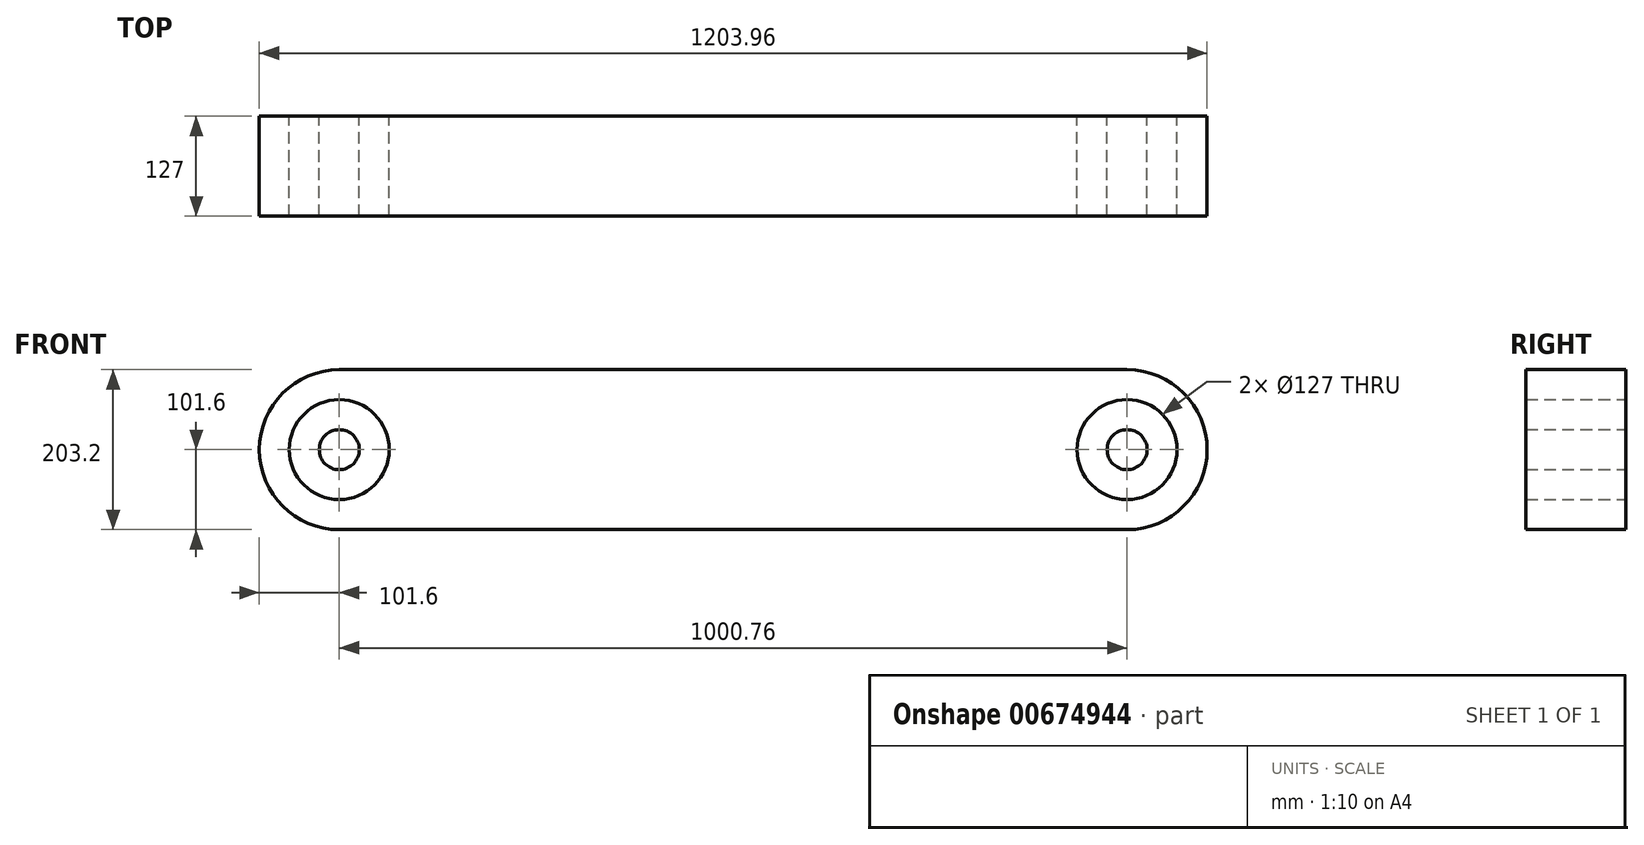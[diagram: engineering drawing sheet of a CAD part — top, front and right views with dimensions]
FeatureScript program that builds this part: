
annotation { "Feature Type Name" : "Feature", "Feature Type Description" : "" }
export const myFeature = defineFeature(function(context is Context, id is Id, definition is map)
    precondition{}
    {
        {
            var Q0;
            Q0=qCreatedBy(makeId("Front.planeOp"),FACE);
            var sketch = newSketch(context, id + "F0", { "sketchPlane" : qUnion([Q0])});
            skLineSegment(sketch, "E0.bottom", {"start": v(0, 0) * mm, "end": v(1000.76, 0) * mm});
            skLineSegment(sketch, "E0.top", {"start": v(0, 203.2) * mm, "end": v(1000.76, 203.2) * mm});
            skArc(sketch, "E1", {"start": v(0, 203.2) * mm, "mid": v(-101.6, 101.6) * mm, "end": v(0, 0) * mm});
            skArc(sketch, "E2", {"start": v(1000.76, 0) * mm, "mid": v(1102.36, 101.6) * mm, "end": v(1000.76, 203.2) * mm});
            skCircle(sketch, "E3", {"center": v(0, 101.6) * mm, "radius": 63.5 * mm});
            skCircle(sketch, "E4", {"center": v(1000.76, 101.6) * mm, "radius": 63.5 * mm});
            skCircle(sketch, "E5", {"center": v(1000.76, 101.6) * mm, "radius": 25.4 * mm});
            skCircle(sketch, "E6", {"center": v(0, 101.6) * mm, "radius": 25.4 * mm});
            skSolve(sketch);
        }
        {
            var Q0;
            Q0=makeQuery(id+"F0.imprint","IMPRINT",FACE,{"disambiguationData":[TD([[makeQuery(id+"F0.imprint","IMPRINT",EDGE,{"derivedFrom":sQuery(id+"F0.wireOp",EDGE,"E0.bottom")}),1.0]])]});
            var Q1;
            Q1=makeQuery(id+"F0.imprint","IMPRINT",FACE,{"disambiguationData":[TD([[makeQuery(id+"F0.imprint","IMPRINT",EDGE,{"derivedFrom":sQuery(id+"F0.wireOp",EDGE,"E6")}),1.0]])]});
            var Q2;
            Q2=makeQuery(id+"F0.imprint","IMPRINT",FACE,{"disambiguationData":[TD([[makeQuery(id+"F0.imprint","IMPRINT",EDGE,{"derivedFrom":sQuery(id+"F0.wireOp",EDGE,"E5")}),1.0]])]});
            extrude(context, id + "F1", {"entities" : qUnion([Q0, Q1, Q2]), "depth" : 127 * mm, "offsetDistance" : 25.4 * mm});
        }
    });
